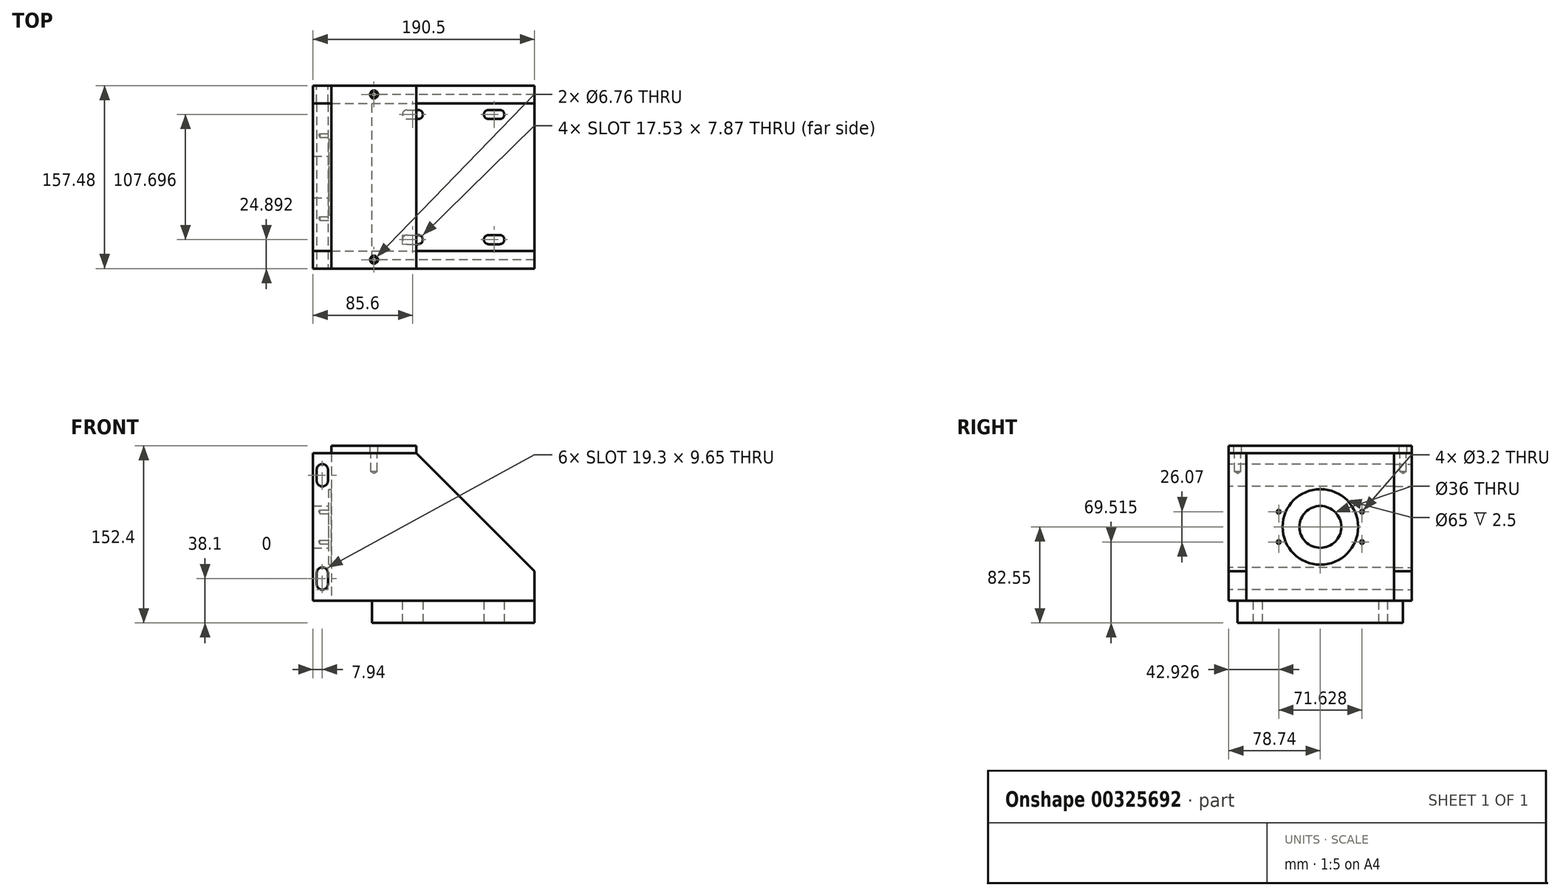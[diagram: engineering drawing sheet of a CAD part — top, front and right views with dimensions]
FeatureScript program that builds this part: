
annotation { "Feature Type Name" : "Feature", "Feature Type Description" : "" }
export const myFeature = defineFeature(function(context is Context, id is Id, definition is map)
    precondition{}
    {
        {
            var Q0;
            Q0=qCreatedBy(makeId("Right.planeOp"),FACE);
            var sketch = newSketch(context, id + "F0", { "sketchPlane" : qUnion([Q0])});
            skLineSegment(sketch, "E0.bottom", {"start": v(-63.5, 63.5) * mm, "end": v(63.5, 63.5) * mm});
            skLineSegment(sketch, "E0.top", {"start": v(-63.5, -63.5) * mm, "end": v(63.5, -63.5) * mm});
            skLineSegment(sketch, "E0.left", {"start": v(-63.5, 63.5) * mm, "end": v(-63.5, -63.5) * mm});
            skLineSegment(sketch, "E0.right", {"start": v(63.5, 63.5) * mm, "end": v(63.5, -63.5) * mm});
            skPoint(sketch, "E0.middle", {"position": v(0, 0) * mm});
            skSolve(sketch);
        }
        {
            var Q0;
            Q0=qSketchRegion(id+"F0",true);
            extrude(context, id + "F1", {"entities" : qUnion([Q0]), "endBound" : BoundingType.SYMMETRIC, "depth" : 15.88 * mm});
        }
        {
            var Q0;
            Q0=makeQuery(id+"F1.opExtrude","CAP_FACE",FACE,{"disambiguationData":[OSD([sQuery(id+"F0.wireOp",EDGE,"E0.bottom"),sQuery(id+"F0.wireOp",EDGE,"E0.top"),sQuery(id+"F0.wireOp",EDGE,"E0.left"),sQuery(id+"F0.wireOp",EDGE,"E0.right")])],"isStart":false});
            var sketch = newSketch(context, id + "F2", { "sketchPlane" : qUnion([Q0])});
            skPoint(sketch, "E1", {"position": v(0, 0) * mm});
            skSolve(sketch);
        }
        {
            var Q0;
            Q0=sQuery(id+"F2.wireOp",VERTEX,"E1");
            var Q1;
            Q1=makeQuery(id+"F1.opExtrude","SWEPT_BODY",BODY,{"disambiguationData":[OSD([sQuery(id+"F0.wireOp",EDGE,"E0.bottom"),sQuery(id+"F0.wireOp",EDGE,"E0.top"),sQuery(id+"F0.wireOp",EDGE,"E0.left"),sQuery(id+"F0.wireOp",EDGE,"E0.right")])]});
            hole(context, id + "F3", {"style" : HoleStyle.C_BORE, "endStyle" : HoleEndStyle.THROUGH, "holeDiameter" : 36 * mm, "cBoreDiameter" : 65 * mm, "cBoreDepth" : 2.5 * mm, "tappedDepth" : 14.3 * mm, "tapClearance" : 3, "locations" : qUnion([Q0]), "scope" : qUnion([Q1])});
        }
        {
            var Q0;
            Q0=makeQuery(id+"F1.opExtrude","CAP_FACE",FACE,{"disambiguationData":[OSD([sQuery(id+"F0.wireOp",EDGE,"E0.bottom"),sQuery(id+"F0.wireOp",EDGE,"E0.top"),sQuery(id+"F0.wireOp",EDGE,"E0.left"),sQuery(id+"F0.wireOp",EDGE,"E0.right")])],"isStart":false});
            var sketch = newSketch(context, id + "F4", { "sketchPlane" : qUnion([Q0])});
            skLineSegment(sketch, "E2", {"start": v(0, 98.6) * mm, "end": v(0, -102.71) * mm, "construction": true});
            skLineSegment(sketch, "E3", {"start": v(0, 0) * mm, "end": v(-134.9, 0) * mm, "construction": true});
            skLineSegment(sketch, "E4", {"start": v(0, 0) * mm, "end": v(-129.05, 46.97) * mm, "construction": true});
            skLineSegment(sketch, "E5.0", {"start": v(-35.81, 98.6) * mm, "end": v(-35.81, -102.71) * mm, "construction": true});
            skPoint(sketch, "E6", {"position": v(-35.81, 13.04) * mm});
            skPoint(sketch, "E7.MirrorP", {"position": v(-35.81, -13.04) * mm});
            skPoint(sketch, "E8.MirrorP", {"position": v(35.81, 13.04) * mm});
            skPoint(sketch, "E9.MirrorP", {"position": v(35.81, -13.04) * mm});
            skSolve(sketch);
        }
        {
            var Q0;
            Q0=sQuery(id+"F4.wireOp",VERTEX,"E6");
            var Q1;
            Q1=sQuery(id+"F4.wireOp",VERTEX,"E7.MirrorP");
            var Q2;
            Q2=sQuery(id+"F4.wireOp",VERTEX,"E8.MirrorP");
            var Q3;
            Q3=sQuery(id+"F4.wireOp",VERTEX,"E9.MirrorP");
            var Q4;
            Q4=makeQuery(id+"F1.opExtrude","SWEPT_BODY",BODY,{"disambiguationData":[OSD([sQuery(id+"F0.wireOp",EDGE,"E0.bottom"),sQuery(id+"F0.wireOp",EDGE,"E0.top"),sQuery(id+"F0.wireOp",EDGE,"E0.left"),sQuery(id+"F0.wireOp",EDGE,"E0.right")])]});
            hole(context, id + "F5", {"style" : HoleStyle.SIMPLE, "endStyle" : HoleEndStyle.BLIND, "standardTappedOrClearance" : lookupTablePath({ "standard" : "ISO", "engagement" : "75%", "pitch" : "0.75 mm", "size" : "M4", "type" : "Tapped" }), "standardBlindInLast" : lookupTablePath({ "standard" : "ISO", "engagement" : "75%", "pitch" : "0.75 mm", "size" : "M4", "type" : "Tapped" }), "holeDiameter" : 3.2 * mm, "showTappedDepth" : true, "holeDepth" : 10 * mm, "tappedDepth" : 7.75 * mm, "tapClearance" : 3, "locations" : qUnion([Q0, Q1, Q2, Q3]), "scope" : qUnion([Q4])});
        }
        {
            var Q0;
            Q0=makeQuery(id+"F1.opExtrude","SWEPT_FACE",FACE,{"disambiguationData":[OSD([sQuery(id+"F0.wireOp",EDGE,"E0.left")])]});
            var sketch = newSketch(context, id + "F6", { "sketchPlane" : qUnion([Q0])});
            skLineSegment(sketch, "E10", {"start": v(0, 89.08) * mm, "end": v(0, -90.33) * mm, "construction": true});
            skPoint(sketch, "E10.endSnap0", {"position": v(0, -63.5) * mm});
            skLineSegment(sketch, "E11", {"start": v(-87.52, 0) * mm, "end": v(87.2, 0) * mm, "construction": true});
            skLineSegment(sketch, "E12.0", {"start": v(-87.52, 44.45) * mm, "end": v(87.2, 44.45) * mm, "construction": true});
            skPoint(sketch, "E13", {"position": v(0, 44.45) * mm});
            skPoint(sketch, "E14.MirrorP", {"position": v(0, -44.45) * mm});
            skSolve(sketch);
        }
        {
            var Q0;
            Q0=sQuery(id+"F6.wireOp",VERTEX,"E13");
            var Q1;
            Q1=sQuery(id+"F6.wireOp",VERTEX,"E14.MirrorP");
            var Q2;
            Q2=makeQuery(id+"F1.opExtrude","SWEPT_BODY",BODY,{"disambiguationData":[OSD([sQuery(id+"F0.wireOp",EDGE,"E0.bottom"),sQuery(id+"F0.wireOp",EDGE,"E0.top"),sQuery(id+"F0.wireOp",EDGE,"E0.left"),sQuery(id+"F0.wireOp",EDGE,"E0.right")])]});
            hole(context, id + "F7", {"style" : HoleStyle.SIMPLE, "endStyle" : HoleEndStyle.BLIND, "standardTappedOrClearance" : lookupTablePath({ "standard" : "ANSI", "engagement" : "75%", "pitch" : "16 tpi", "size" : "3/8", "type" : "Tapped" }), "standardBlindInLast" : lookupTablePath({ "standard" : "ANSI", "engagement" : "75%", "pitch" : "16 tpi", "size" : "3/8", "type" : "Tapped" }), "holeDiameter" : 7.94 * mm, "showTappedDepth" : true, "holeDepth" : 16.83 * mm, "tappedDepth" : 12.06 * mm, "tapClearance" : 3, "locations" : qUnion([Q0, Q1]), "scope" : qUnion([Q2]), "majorDiameter" : 9.53 * mm});
        }
        {
            var Q0;
            Q0=makeQuery(id+"F1.opExtrude","SWEPT_FACE",FACE,{"disambiguationData":[OSD([sQuery(id+"F0.wireOp",EDGE,"E0.left")])]});
            var sketch = newSketch(context, id + "F8", { "sketchPlane" : qUnion([Q0])});
            skLineSegment(sketch, "E15.bottom", {"start": v(-7.94, 63.5) * mm, "end": v(182.56, 63.5) * mm});
            skLineSegment(sketch, "E15.top", {"start": v(-7.94, -63.5) * mm, "end": v(182.56, -63.5) * mm});
            skLineSegment(sketch, "E15.left", {"start": v(-7.94, 63.5) * mm, "end": v(-7.94, -63.5) * mm});
            skLineSegment(sketch, "E15.right", {"start": v(182.56, 63.5) * mm, "end": v(182.56, -63.5) * mm});
            skSolve(sketch);
        }
        {
            var Q0;
            Q0=qSketchRegion(id+"F8",true);
            extrude(context, id + "F9", {"entities" : qUnion([Q0]), "depth" : 15.24 * mm});
        }
        {
            var Q0;
            Q0=makeQuery(id+"F9.opExtrude","CAP_FACE",FACE,{"disambiguationData":[OSD([sQuery(id+"F8.wireOp",EDGE,"E15.bottom"),sQuery(id+"F8.wireOp",EDGE,"E15.top"),sQuery(id+"F8.wireOp",EDGE,"E15.left"),sQuery(id+"F8.wireOp",EDGE,"E15.right")])],"isStart":false});
            var sketch = newSketch(context, id + "F10", { "sketchPlane" : qUnion([Q0])});
            skCircle(sketch, "E16.0", {"center": v(0, 44.45) * mm, "radius": 3.97 * mm, "construction": true});
            skCircle(sketch, "E17.0", {"center": v(0, -44.45) * mm, "radius": 3.97 * mm, "construction": true});
            skLineSegment(sketch, "E18", {"start": v(-10.52, 44.45) * mm, "end": v(11.32, 44.45) * mm, "construction": true});
            skLineSegment(sketch, "E19", {"start": v(0, 0) * mm, "end": v(-27.4, 0) * mm, "construction": true});
            skPoint(sketch, "E20.orphan", {"position": v(-15.83, -44.45) * mm});
            skLineSegment(sketch, "E21", {"start": v(0, 49.28) * mm, "end": v(0, 39.62) * mm});
            skArc(sketch, "E22.0.startCap", {"start": v(-4.83, 49.28) * mm, "mid": v(0, 54.1) * mm, "end": v(4.83, 49.28) * mm});
            skArc(sketch, "E22.0.endCap", {"start": v(4.83, 39.62) * mm, "mid": v(0, 34.8) * mm, "end": v(-4.83, 39.62) * mm});
            skLineSegment(sketch, "E22.0.left", {"start": v(4.83, 49.28) * mm, "end": v(4.83, 39.62) * mm});
            skLineSegment(sketch, "E22.0.right", {"start": v(-4.83, 49.28) * mm, "end": v(-4.83, 39.62) * mm});
            skLineSegment(sketch, "E23.MirrorCS", {"start": v(0, -49.28) * mm, "end": v(0, -39.62) * mm});
            skLineSegment(sketch, "E24.MirrorCS", {"start": v(-4.83, -49.28) * mm, "end": v(-4.83, -39.62) * mm});
            skLineSegment(sketch, "E25.MirrorCS", {"start": v(4.83, -49.28) * mm, "end": v(4.83, -39.62) * mm});
            skLineSegment(sketch, "E26.MirrorCS", {"start": v(-10.52, -44.45) * mm, "end": v(11.32, -44.45) * mm, "construction": true});
            skArc(sketch, "E27.MirrorCS", {"start": v(4.83, -39.62) * mm, "mid": v(0, -34.8) * mm, "end": v(-4.83, -39.62) * mm});
            skArc(sketch, "E28.MirrorCS", {"start": v(-4.83, -49.28) * mm, "mid": v(0, -54.1) * mm, "end": v(4.83, -49.28) * mm});
            skSolve(sketch);
        }
        {
            var Q0;
            Q0=qSketchRegion(id+"F10",true);
            extrude(context, id + "F11", {"entities" : qUnion([Q0]), "operationType" : NewBodyOperationType.REMOVE, "endBound" : BoundingType.THROUGH_ALL, "oppositeDirection" : true, "depth" : 25.4 * mm});
        }
        {
            var Q0;
            Q0=makeQuery(id+"F9.opExtrude","SWEPT_EDGE",EDGE,{"disambiguationData":[OSD([sQuery(id+"F8.wireOp",EDGE,"E15.bottom"),sQuery(id+"F8.wireOp",EDGE,"E15.right")])]});
            chamfer(context, id + "F12", {"entities" : qUnion([Q0]), "width" : 101.6 * mm, "tangentPropagation" : true});
        }
        {
            var Q0;
            Q0=makeQuery(id+"F9.opExtrude","SWEPT_FACE",FACE,{"disambiguationData":[OSD([sQuery(id+"F8.wireOp",EDGE,"E15.top")])]});
            var sketch = newSketch(context, id + "F13", { "sketchPlane" : qUnion([Q0])});
            skLineSegment(sketch, "E29", {"start": v(-146.6, 0) * mm, "end": v(258.5, 0) * mm, "construction": true});
            skLineSegment(sketch, "E30", {"start": v(182.56, 71.12) * mm, "end": v(-86.58, 71.12) * mm, "construction": true});
            skLineSegment(sketch, "E31.MirrorCS", {"start": v(182.56, -71.12) * mm, "end": v(-86.58, -71.12) * mm, "construction": true});
            skLineSegment(sketch, "E32.bottom", {"start": v(182.56, 71.12) * mm, "end": v(42.86, 71.12) * mm});
            skLineSegment(sketch, "E32.top", {"start": v(182.56, -71.12) * mm, "end": v(42.86, -71.12) * mm});
            skLineSegment(sketch, "E32.left", {"start": v(182.56, 71.12) * mm, "end": v(182.56, -71.12) * mm});
            skLineSegment(sketch, "E32.right", {"start": v(42.86, 71.12) * mm, "end": v(42.86, -71.12) * mm});
            skSolve(sketch);
        }
        {
            var Q0;
            Q0=qSketchRegion(id+"F13",true);
            extrude(context, id + "F14", {"entities" : qUnion([Q0]), "depth" : 19.05 * mm});
        }
        {
            var Q0;
            Q0=makeQuery(id+"F9.opExtrude","SWEPT_BODY",BODY,{"disambiguationData":[OSD([sQuery(id+"F8.wireOp",EDGE,"E15.bottom"),sQuery(id+"F8.wireOp",EDGE,"E15.top"),sQuery(id+"F8.wireOp",EDGE,"E15.left"),sQuery(id+"F8.wireOp",EDGE,"E15.right")])]});
            var Q1;
            Q1=qCreatedBy(makeId("Front.planeOp"),FACE);
            mirror(context, id + "F15", {"entities" : qUnion([Q0]), "mirrorPlane" : qUnion([Q1])});
        }
        {
            var Q0;
            Q0=makeQuery(id+"F14.opExtrude","CAP_FACE",FACE,{"disambiguationData":[OSD([sQuery(id+"F13.wireOp",EDGE,"E32.bottom"),sQuery(id+"F13.wireOp",EDGE,"E32.top"),sQuery(id+"F13.wireOp",EDGE,"E32.left"),sQuery(id+"F13.wireOp",EDGE,"E32.right")])],"isStart":false});
            var sketch = newSketch(context, id + "F16", { "sketchPlane" : qUnion([Q0])});
            skLineSegment(sketch, "E33", {"start": v(112.71, 71.12) * mm, "end": v(112.71, -71.12) * mm, "construction": true});
            skLineSegment(sketch, "E34", {"start": v(194.6, 0) * mm, "end": v(-98.27, 0) * mm, "construction": true});
            skPoint(sketch, "E34.endSnap0", {"position": v(182.56, 0) * mm});
            skLineSegment(sketch, "E35.0", {"start": v(77.66, 71.12) * mm, "end": v(77.66, -71.12) * mm, "construction": true});
            skLineSegment(sketch, "E36", {"start": v(77.66, 53.85) * mm, "end": v(72.83, 53.85) * mm, "construction": true});
            skLineSegment(sketch, "E37", {"start": v(72.83, 53.85) * mm, "end": v(82.49, 53.85) * mm});
            skArc(sketch, "E38.0.startCap", {"start": v(72.83, 49.91) * mm, "mid": v(68.9, 53.85) * mm, "end": v(72.83, 57.78) * mm});
            skArc(sketch, "E38.0.endCap", {"start": v(82.49, 57.78) * mm, "mid": v(86.42, 53.85) * mm, "end": v(82.49, 49.91) * mm});
            skLineSegment(sketch, "E38.0.left", {"start": v(72.83, 57.78) * mm, "end": v(82.49, 57.78) * mm});
            skLineSegment(sketch, "E38.0.right", {"start": v(72.83, 49.91) * mm, "end": v(82.49, 49.91) * mm});
            skLineSegment(sketch, "E39.MirrorCS", {"start": v(147.76, 53.85) * mm, "end": v(152.6, 53.85) * mm, "construction": true});
            skLineSegment(sketch, "E40.MirrorCS", {"start": v(152.6, 49.91) * mm, "end": v(142.94, 49.91) * mm});
            skLineSegment(sketch, "E41.MirrorCS", {"start": v(152.6, 53.85) * mm, "end": v(142.94, 53.85) * mm});
            skArc(sketch, "E42.MirrorCS", {"start": v(152.6, 49.91) * mm, "mid": v(156.53, 53.85) * mm, "end": v(152.6, 57.78) * mm});
            skArc(sketch, "E43.MirrorCS", {"start": v(142.94, 57.78) * mm, "mid": v(139, 53.85) * mm, "end": v(142.94, 49.91) * mm});
            skLineSegment(sketch, "E44.MirrorCS", {"start": v(152.6, 57.78) * mm, "end": v(142.94, 57.78) * mm});
            skLineSegment(sketch, "E45.MirrorCS", {"start": v(77.66, -53.85) * mm, "end": v(72.83, -53.85) * mm, "construction": true});
            skLineSegment(sketch, "E46.MirrorCS", {"start": v(72.83, -53.85) * mm, "end": v(82.49, -53.85) * mm});
            skLineSegment(sketch, "E47.MirrorCS", {"start": v(72.83, -57.78) * mm, "end": v(82.49, -57.78) * mm});
            skLineSegment(sketch, "E48.MirrorCS", {"start": v(72.83, -49.91) * mm, "end": v(82.49, -49.91) * mm});
            skLineSegment(sketch, "E49.MirrorCS", {"start": v(152.6, -53.85) * mm, "end": v(142.94, -53.85) * mm});
            skLineSegment(sketch, "E50.MirrorCS", {"start": v(147.76, -53.85) * mm, "end": v(152.6, -53.85) * mm, "construction": true});
            skArc(sketch, "E51.MirrorCS", {"start": v(72.83, -49.91) * mm, "mid": v(68.9, -53.85) * mm, "end": v(72.83, -57.78) * mm});
            skArc(sketch, "E52.MirrorCS", {"start": v(152.6, -49.91) * mm, "mid": v(156.53, -53.85) * mm, "end": v(152.6, -57.78) * mm});
            skArc(sketch, "E53.MirrorCS", {"start": v(82.49, -57.78) * mm, "mid": v(86.42, -53.85) * mm, "end": v(82.49, -49.91) * mm});
            skLineSegment(sketch, "E54.MirrorCS", {"start": v(152.6, -57.78) * mm, "end": v(142.94, -57.78) * mm});
            skArc(sketch, "E55.MirrorCS", {"start": v(142.94, -57.78) * mm, "mid": v(139, -53.85) * mm, "end": v(142.94, -49.91) * mm});
            skLineSegment(sketch, "E56.MirrorCS", {"start": v(152.6, -49.91) * mm, "end": v(142.94, -49.91) * mm});
            skSolve(sketch);
        }
        {
            var Q0;
            Q0=qSketchRegion(id+"F16",true);
            extrude(context, id + "F17", {"entities" : qUnion([Q0]), "operationType" : NewBodyOperationType.REMOVE, "endBound" : BoundingType.THROUGH_ALL, "oppositeDirection" : true, "depth" : 25.4 * mm});
        }
        {
            var Q0;
            Q0=makeQuery(id+"F15.opPattern","COPY",FACE,{"derivedFrom":makeQuery(id+"F9.opExtrude","SWEPT_FACE",FACE,{"disambiguationData":[OSD([sQuery(id+"F8.wireOp",EDGE,"E15.bottom")])]}),"instanceName":"1"});
            var sketch = newSketch(context, id + "F18", { "sketchPlane" : qUnion([Q0])});
            skLineSegment(sketch, "E57.0.0", {"start": v(80.96, 78.74) * mm, "end": v(-7.94, 78.74) * mm, "construction": true});
            skLineSegment(sketch, "E57.0.1", {"start": v(-7.94, 78.74) * mm, "end": v(-7.94, 63.5) * mm, "construction": true});
            skLineSegment(sketch, "E57.0.2", {"start": v(-7.94, 63.5) * mm, "end": v(80.96, 63.5) * mm, "construction": true});
            skLineSegment(sketch, "E57.0.3", {"start": v(80.96, 63.5) * mm, "end": v(80.96, 78.74) * mm, "construction": true});
            skLineSegment(sketch, "E58.0.0", {"start": v(-7.94, -78.74) * mm, "end": v(80.96, -78.74) * mm, "construction": true});
            skLineSegment(sketch, "E58.0.1", {"start": v(80.96, -78.74) * mm, "end": v(80.96, -63.5) * mm, "construction": true});
            skLineSegment(sketch, "E58.0.2", {"start": v(80.96, -63.5) * mm, "end": v(-7.94, -63.5) * mm, "construction": true});
            skLineSegment(sketch, "E58.0.3", {"start": v(-7.94, -63.5) * mm, "end": v(-7.94, -78.74) * mm, "construction": true});
            skLineSegment(sketch, "E59", {"start": v(80.96, 71.12) * mm, "end": v(7.94, 71.12) * mm, "construction": true});
            skLineSegment(sketch, "E60", {"start": v(80.96, -71.12) * mm, "end": v(7.94, -71.12) * mm, "construction": true});
            skLineSegment(sketch, "E61.0.1", {"start": v(7.94, -78.74) * mm, "end": v(7.94, 78.74) * mm, "construction": true});
            skLineSegment(sketch, "E61.0.3", {"start": v(7.94, 63.5) * mm, "end": v(7.94, -63.5) * mm, "construction": true});
            skPoint(sketch, "E62.orphan", {"position": v(7.94, 63.5) * mm});
            skPoint(sketch, "E63.orphan", {"position": v(7.94, -63.5) * mm});
            skPoint(sketch, "E64.orphan", {"position": v(-7.94, 71.12) * mm});
            skPoint(sketch, "E65.orphan", {"position": v(-7.94, -71.12) * mm});
            skPoint(sketch, "E66", {"position": v(44.45, 71.12) * mm});
            skPoint(sketch, "E67", {"position": v(44.45, -71.12) * mm});
            skSolve(sketch);
        }
        {
            var Q0;
            Q0=sQuery(id+"F18.wireOp",VERTEX,"E66");
            var Q1;
            Q1=sQuery(id+"F18.wireOp",VERTEX,"E67");
            var Q2;
            Q2=makeQuery(id+"F9.opExtrude","SWEPT_BODY",BODY,{"disambiguationData":[OSD([sQuery(id+"F8.wireOp",EDGE,"E15.bottom"),sQuery(id+"F8.wireOp",EDGE,"E15.top"),sQuery(id+"F8.wireOp",EDGE,"E15.left"),sQuery(id+"F8.wireOp",EDGE,"E15.right")])]});
            var Q3;
            Q3=makeQuery(id+"F15.opPattern","COPY",BODY,{"derivedFrom":makeQuery(id+"F9.opExtrude","SWEPT_BODY",BODY,{"disambiguationData":[OSD([sQuery(id+"F8.wireOp",EDGE,"E15.bottom"),sQuery(id+"F8.wireOp",EDGE,"E15.top"),sQuery(id+"F8.wireOp",EDGE,"E15.left"),sQuery(id+"F8.wireOp",EDGE,"E15.right")])]}),"instanceName":"1"});
            hole(context, id + "F19", {"style" : HoleStyle.SIMPLE, "endStyle" : HoleEndStyle.BLIND, "standardTappedOrClearance" : lookupTablePath({ "standard" : "ANSI", "engagement" : "75%", "pitch" : "20 tpi", "size" : "1/4", "type" : "Tapped" }), "standardBlindInLast" : lookupTablePath({ "standard" : "ANSI", "engagement" : "75%", "pitch" : "20 tpi", "size" : "1/4", "type" : "Tapped" }), "holeDiameter" : 5.1 * mm, "showTappedDepth" : true, "holeDepth" : 15.86 * mm, "tappedDepth" : 12.05 * mm, "tapClearance" : 3, "locations" : qUnion([Q0, Q1]), "scope" : qUnion([Q2, Q3]), "majorDiameter" : 6.35 * mm});
        }
        {
            var Q0;
            Q0=makeQuery(id+"F15.opPattern","COPY",FACE,{"derivedFrom":makeQuery(id+"F9.opExtrude","SWEPT_FACE",FACE,{"disambiguationData":[OSD([sQuery(id+"F8.wireOp",EDGE,"E15.bottom")])]}),"instanceName":"1"});
            var sketch = newSketch(context, id + "F20", { "sketchPlane" : qUnion([Q0])});
            skLineSegment(sketch, "E68.0.0", {"start": v(80.96, 78.74) * mm, "end": v(-7.94, 78.74) * mm, "construction": true});
            skLineSegment(sketch, "E68.0.1", {"start": v(-7.94, 78.74) * mm, "end": v(-7.94, 63.5) * mm, "construction": true});
            skLineSegment(sketch, "E68.0.2", {"start": v(-7.94, 63.5) * mm, "end": v(80.96, 63.5) * mm, "construction": true});
            skLineSegment(sketch, "E68.0.3", {"start": v(80.96, 63.5) * mm, "end": v(80.96, 78.74) * mm, "construction": true});
            skLineSegment(sketch, "E69.0.0", {"start": v(-7.94, -78.74) * mm, "end": v(80.96, -78.74) * mm, "construction": true});
            skLineSegment(sketch, "E69.0.1", {"start": v(80.96, -78.74) * mm, "end": v(80.96, -63.5) * mm, "construction": true});
            skLineSegment(sketch, "E69.0.2", {"start": v(80.96, -63.5) * mm, "end": v(-7.94, -63.5) * mm, "construction": true});
            skLineSegment(sketch, "E69.0.3", {"start": v(-7.94, -63.5) * mm, "end": v(-7.94, -78.74) * mm, "construction": true});
            skLineSegment(sketch, "E70.0.0", {"start": v(-7.94, 63.5) * mm, "end": v(-7.94, -63.5) * mm, "construction": true});
            skLineSegment(sketch, "E70.0.1", {"start": v(-7.94, -63.5) * mm, "end": v(7.94, -63.5) * mm, "construction": true});
            skLineSegment(sketch, "E70.0.2", {"start": v(7.94, -63.5) * mm, "end": v(7.94, 63.5) * mm, "construction": true});
            skLineSegment(sketch, "E70.0.3", {"start": v(7.94, 63.5) * mm, "end": v(-7.94, 63.5) * mm, "construction": true});
            skLineSegment(sketch, "E71.bottom", {"start": v(80.96, 78.74) * mm, "end": v(7.94, 78.74) * mm});
            skLineSegment(sketch, "E71.top", {"start": v(80.96, -78.74) * mm, "end": v(7.94, -78.74) * mm});
            skLineSegment(sketch, "E71.left", {"start": v(80.96, 78.74) * mm, "end": v(80.96, -78.74) * mm});
            skLineSegment(sketch, "E71.right", {"start": v(7.94, 78.74) * mm, "end": v(7.94, -78.74) * mm});
            skSolve(sketch);
        }
        {
            var Q0;
            Q0=qSketchRegion(id+"F20",true);
            extrude(context, id + "F21", {"entities" : qUnion([Q0]), "depth" : 6.35 * mm});
        }
        {
            var Q0;
            Q0=makeQuery(id+"F21.opExtrude","CAP_FACE",FACE,{"disambiguationData":[OSD([sQuery(id+"F20.wireOp",EDGE,"E71.bottom"),sQuery(id+"F20.wireOp",EDGE,"E71.top"),sQuery(id+"F20.wireOp",EDGE,"E71.left"),sQuery(id+"F20.wireOp",EDGE,"E71.right")])],"isStart":false});
            var sketch = newSketch(context, id + "F22", { "sketchPlane" : qUnion([Q0])});
            skCircle(sketch, "E72.0", {"center": v(44.45, 71.12) * mm, "radius": 2.55 * mm, "construction": true});
            skCircle(sketch, "E73.0", {"center": v(44.45, -71.12) * mm, "radius": 2.55 * mm, "construction": true});
            skSolve(sketch);
        }
        {
            var Q0;
            Q0=sQuery(id+"F22.wireOp",VERTEX,"E72.0.center");
            var Q1;
            Q1=sQuery(id+"F22.wireOp",VERTEX,"E73.0.center");
            var Q2;
            Q2=makeQuery(id+"F21.opExtrude","SWEPT_BODY",BODY,{"disambiguationData":[OSD([sQuery(id+"F20.wireOp",EDGE,"E71.bottom"),sQuery(id+"F20.wireOp",EDGE,"E71.top"),sQuery(id+"F20.wireOp",EDGE,"E71.left"),sQuery(id+"F20.wireOp",EDGE,"E71.right")])]});
            hole(context, id + "F23", {"style" : HoleStyle.SIMPLE, "endStyle" : HoleEndStyle.BLIND, "standardTappedOrClearance" : lookupTablePath({ "standard" : "ANSI", "fit" : "Normal (ASME)", "size" : "1/4", "type" : "Clearance" }), "standardBlindInLast" : lookupTablePath({ "fit" : "Free", "standard" : "ANSI", "size" : "1/4", "type" : "Clearance" }), "holeDiameter" : 6.76 * mm, "holeDepth" : 15.88 * mm, "tappedDepth" : 12.06 * mm, "tapClearance" : 3, "locations" : qUnion([Q0, Q1]), "scope" : qUnion([Q2])});
        }
    });
